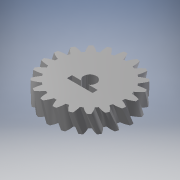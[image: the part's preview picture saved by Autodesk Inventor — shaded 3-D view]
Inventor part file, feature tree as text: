
AUTODESK INVENTOR PART (.ipt)
format: ipt  version: 2017 SP1 (Build 210196100, 196)  size: 850,432 bytes
history: native  units: mm (DEFAULTED — no unit token found)
features: plane x3, other x3, sketch x3, extrude x2
ambient origin geometry x8: Origin, YZ Plane, XZ Plane, XY Plane, X Axis, Y Axis, Z Axis, Center Point
bodies: Solid1 (feature_tree)
feature tree (11):
  extrude  "Extrusion1"  Depth=7.0mm TaperAngle=0.0deg
  plane  "Work Plane2"
  plane  "Work Plane8"
  plane  "Work Plane9"
  other  "Engrenage cylindrique"
  extrude  "Extrusion2"  Depth=10.0mm TaperAngle=0.0deg
  sketch  "Sketch1"  dims[d0=32.749068mm d1=7.0mm d2=0.0mm]
  sketch  "Sketch2"  dims[d3=30.066593mm d4=10.0mm d5=0.0mm d16=30.066593mm d17=0.0mm d34=1.570796mm d39=0.0mm d41=0.0mm d43=30.066593mm d46=30.066593mm d47=0.0mm d48=0.0mm d49=5.0mm d50=10.0mm d51=5.0mm d52=2.0mm d53=2.0mm d54=8.0mm d55=0.0mm]
  other  "Srf1"
  sketch  "Esquisse3"
  other  "Diamètre primitif"
